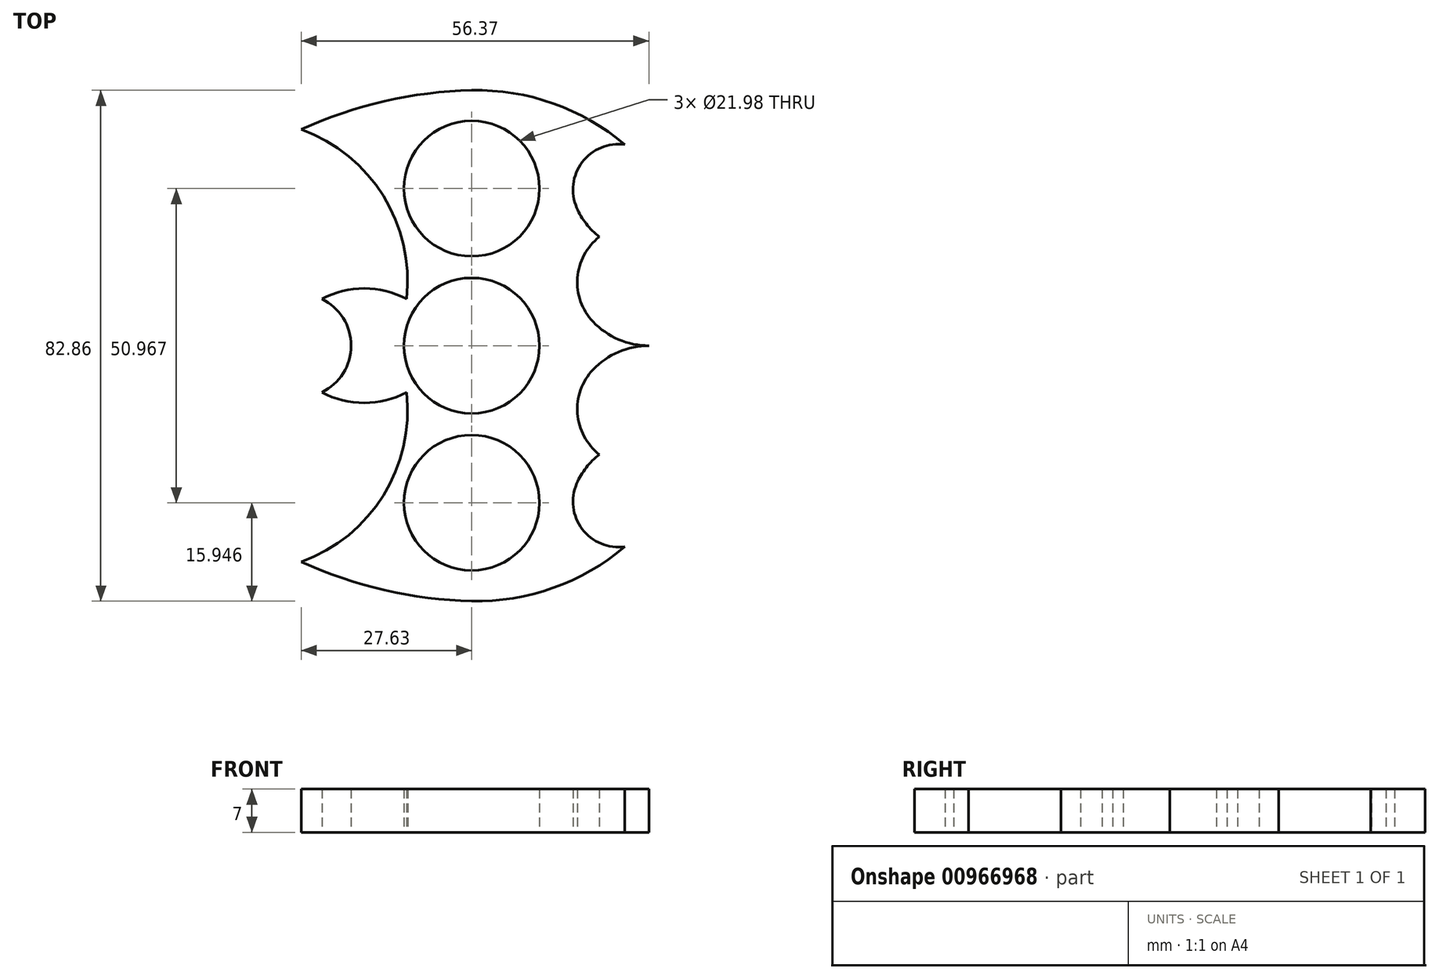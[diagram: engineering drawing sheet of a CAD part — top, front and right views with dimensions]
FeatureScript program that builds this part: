
annotation { "Feature Type Name" : "Feature", "Feature Type Description" : "" }
export const myFeature = defineFeature(function(context is Context, id is Id, definition is map)
    precondition{}
    {
        {
            var Q0;
            Q0=qCreatedBy(makeId("Top.planeOp"),FACE);
            var sketch = newSketch(context, id + "F0", { "sketchPlane" : qUnion([Q0])});
            skCircle(sketch, "E0", {"center": v(0, 0) * mm, "radius": 11 * mm});
            skCircle(sketch, "E1", {"center": v(0, 25.48) * mm, "radius": 11 * mm});
            skCircle(sketch, "E2", {"center": v(0, -25.48) * mm, "radius": 11 * mm});
            skLineSegment(sketch, "E3", {"start": v(0, 25.48) * mm, "end": v(0, -25.48) * mm, "construction": true});
            skLineSegment(sketch, "E4.bottom", {"start": v(-29.85, 57.15) * mm, "end": v(29.85, 57.15) * mm, "construction": true});
            skLineSegment(sketch, "E4.top", {"start": v(-29.85, -57.15) * mm, "end": v(29.85, -57.15) * mm, "construction": true});
            skLineSegment(sketch, "E4.left", {"start": v(-29.84, 57.15) * mm, "end": v(-29.85, -57.15) * mm, "construction": true});
            skLineSegment(sketch, "E4.right", {"start": v(29.85, 57.15) * mm, "end": v(29.84, -57.15) * mm, "construction": true});
            skPoint(sketch, "E5", {"position": v(0, 57.15) * mm});
            skPoint(sketch, "E6", {"position": v(-29.85, 0) * mm});
            skSolve(sketch);
        }
        {
            var Q0;
            Q0=qCreatedBy(makeId("Top.planeOp"),FACE);
            var sketch = newSketch(context, id + "F1", { "sketchPlane" : qUnion([Q0])});
            skCircle(sketch, "E7", {"center": v(0, 25.48) * mm, "radius": 11 * mm});
            skCircle(sketch, "E8", {"center": v(0, 0) * mm, "radius": 11 * mm});
            skCircle(sketch, "E9", {"center": v(0, -25.48) * mm, "radius": 11 * mm});
            skLineSegment(sketch, "E10.bottom", {"start": v(-29.85, 57.15) * mm, "end": v(29.84, 57.15) * mm, "construction": true});
            skLineSegment(sketch, "E10.top", {"start": v(-29.85, -57.15) * mm, "end": v(29.84, -57.15) * mm, "construction": true});
            skLineSegment(sketch, "E10.left", {"start": v(-29.85, 57.15) * mm, "end": v(-29.85, -57.15) * mm, "construction": true});
            skLineSegment(sketch, "E10.right", {"start": v(29.85, 57.15) * mm, "end": v(29.85, -57.15) * mm, "construction": true});
            skPoint(sketch, "E11", {"position": v(-29.85, 0) * mm});
            skPoint(sketch, "E12", {"position": v(0, 57.15) * mm});
            skArc(sketch, "E13", {"start": v(24.82, 32.61) * mm, "mid": v(13.22, 39.3) * mm, "end": v(0, 41.42) * mm});
            skArc(sketch, "E14", {"start": v(0, 41.42) * mm, "mid": v(-14.14, 39.66) * mm, "end": v(-27.63, 35.07) * mm});
            skArc(sketch, "E15", {"start": v(-10.56, 7.57) * mm, "mid": v(-14.32, 24.28) * mm, "end": v(-27.63, 35.07) * mm});
            skArc(sketch, "E16", {"start": v(-10.56, 7.57) * mm, "mid": v(-17.43, 9.29) * mm, "end": v(-24.3, 7.57) * mm});
            skArc(sketch, "E17", {"start": v(-19.55, 0) * mm, "mid": v(-20.83, 4.47) * mm, "end": v(-24.3, 7.57) * mm});
            skArc(sketch, "E18", {"start": v(24.82, 32.61) * mm, "mid": v(17.93, 29.77) * mm, "end": v(17.03, 22.37) * mm});
            skArc(sketch, "E19", {"start": v(17.03, 22.37) * mm, "mid": v(18.57, 19.78) * mm, "end": v(20.72, 17.66) * mm});
            skArc(sketch, "E20", {"start": v(20.72, 17.66) * mm, "mid": v(17.15, 11) * mm, "end": v(19.69, 3.88) * mm});
            skArc(sketch, "E21", {"start": v(19.69, 3.88) * mm, "mid": v(23.81, 1.01) * mm, "end": v(28.74, 0) * mm});
            skLineSegment(sketch, "E22", {"start": v(28.74, 0) * mm, "end": v(51.39, 0) * mm, "construction": true});
            skLineSegment(sketch, "E23", {"start": v(-19.55, 0) * mm, "end": v(-19.55, -18.25) * mm, "construction": true});
            skArc(sketch, "E24.MirrorCS", {"start": v(-19.55, 0) * mm, "mid": v(-20.83, -4.47) * mm, "end": v(-24.3, -7.57) * mm});
            skArc(sketch, "E25.MirrorCS", {"start": v(-10.56, -7.57) * mm, "mid": v(-17.43, -9.29) * mm, "end": v(-24.3, -7.57) * mm});
            skArc(sketch, "E26.MirrorCS", {"start": v(-10.56, -7.57) * mm, "mid": v(-14.32, -24.28) * mm, "end": v(-27.63, -35.07) * mm});
            skArc(sketch, "E27.MirrorCS", {"start": v(0, -41.42) * mm, "mid": v(-14.14, -39.66) * mm, "end": v(-27.63, -35.07) * mm});
            skArc(sketch, "E28.MirrorCS", {"start": v(24.82, -32.61) * mm, "mid": v(13.22, -39.3) * mm, "end": v(0, -41.42) * mm});
            skArc(sketch, "E29.MirrorCS", {"start": v(24.82, -32.61) * mm, "mid": v(17.93, -29.77) * mm, "end": v(17.03, -22.37) * mm});
            skArc(sketch, "E30.MirrorCS", {"start": v(20.72, -17.66) * mm, "mid": v(17.15, -11) * mm, "end": v(19.69, -3.88) * mm});
            skArc(sketch, "E31.MirrorCS", {"start": v(17.03, -22.37) * mm, "mid": v(18.57, -19.78) * mm, "end": v(20.72, -17.66) * mm});
            skArc(sketch, "E32.MirrorCS", {"start": v(19.69, -3.88) * mm, "mid": v(23.81, -1.01) * mm, "end": v(28.74, 0) * mm});
            skSolve(sketch);
        }
        {
            var Q0;
            Q0 = qSketchRegion(id + "F1", true);
            extrude(context, id + "F2", {"entities" : qUnion([Q0]), "depth" : 7 * mm, "offsetDistance" : 25.4 * mm});
        }
    });
